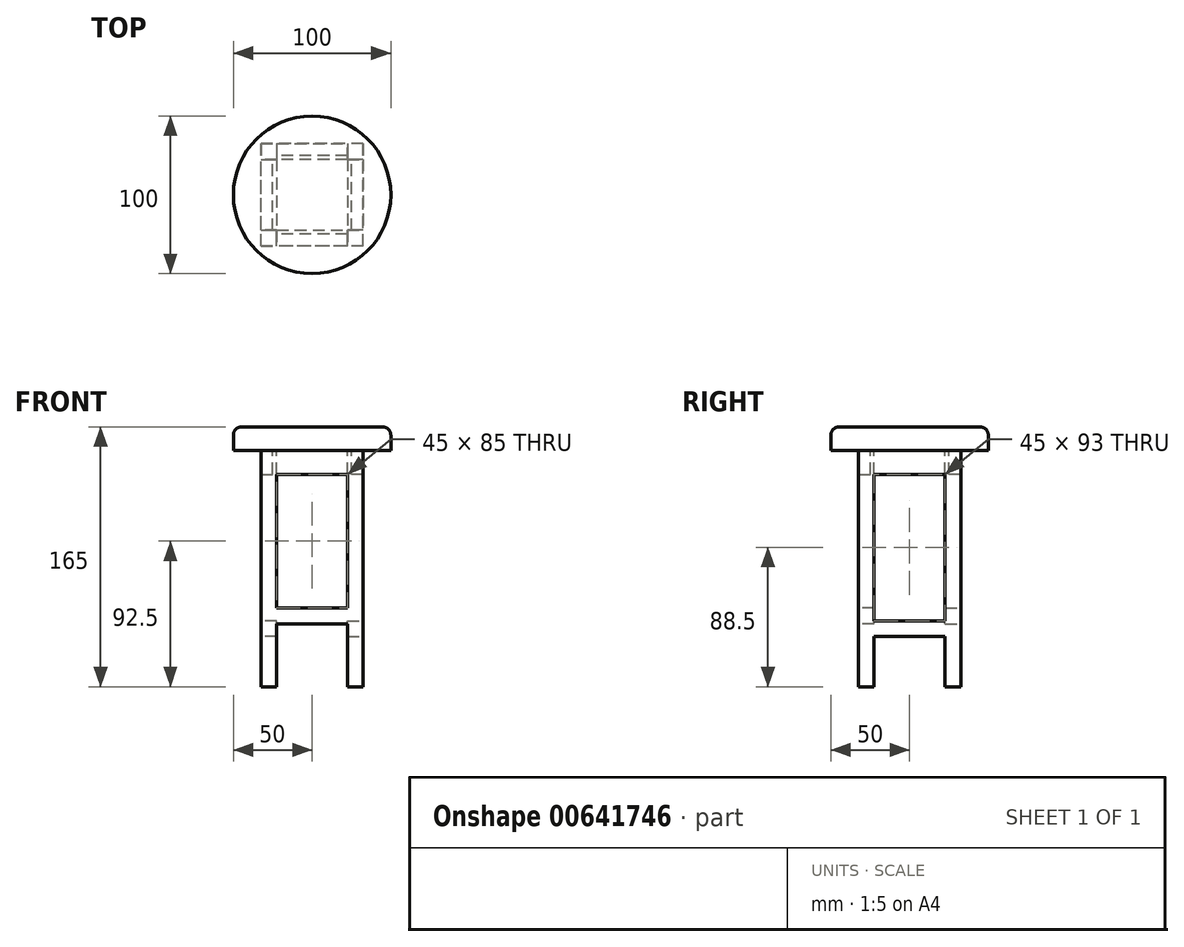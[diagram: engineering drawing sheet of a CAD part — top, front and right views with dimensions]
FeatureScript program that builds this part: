
annotation { "Feature Type Name" : "Feature", "Feature Type Description" : "" }
export const myFeature = defineFeature(function(context is Context, id is Id, definition is map)
    precondition{}
    {
        {
            var Q0;
            Q0=qCreatedBy(makeId("Top.planeOp"),FACE);
            var sketch = newSketch(context, id + "F0", { "sketchPlane" : qUnion([Q0])});
            skCircle(sketch, "E0", {"center": v(0, 0) * mm, "radius": 50 * mm});
            skSolve(sketch);
        }
        {
            var Q0;
            Q0=makeQuery(id+"F0.imprint","IMPRINT",FACE,{"disambiguationData":[TD([[makeQuery(id+"F0.imprint","IMPRINT",EDGE,{"derivedFrom":sQuery(id+"F0.wireOp",EDGE,"E0")}),1.0]])]});
            extrude(context, id + "F1", {"entities" : qUnion([Q0]), "depth" : 15 * mm, "offsetDistance" : 25 * mm});
        }
        {
            var Q0;
            Q0=makeQuery(id+"F1.opExtrude","CAP_FACE",FACE,{"disambiguationData":[OSD([sQuery(id+"F0.wireOp",EDGE,"E0")])],"isStart":true});
            var sketch = newSketch(context, id + "F2", { "sketchPlane" : qUnion([Q0])});
            skLineSegment(sketch, "E1.bottom", {"start": v(32.5, 32.5) * mm, "end": v(-32.5, 32.5) * mm});
            skLineSegment(sketch, "E1.top", {"start": v(32.5, -32.5) * mm, "end": v(-32.5, -32.5) * mm});
            skLineSegment(sketch, "E1.left", {"start": v(32.5, 32.5) * mm, "end": v(32.5, -32.5) * mm});
            skLineSegment(sketch, "E1.right", {"start": v(-32.5, 32.5) * mm, "end": v(-32.5, -32.5) * mm});
            skPoint(sketch, "E1.middle", {"position": v(0, 0) * mm});
            skLineSegment(sketch, "E2.bottom", {"start": v(-32.5, 32.5) * mm, "end": v(-22.5, 32.5) * mm});
            skLineSegment(sketch, "E2.top", {"start": v(-32.5, 22.5) * mm, "end": v(-22.5, 22.5) * mm});
            skLineSegment(sketch, "E2.left", {"start": v(-32.5, 32.5) * mm, "end": v(-32.5, 22.5) * mm});
            skLineSegment(sketch, "E2.right", {"start": v(-22.5, 32.5) * mm, "end": v(-22.5, 22.5) * mm});
            skLineSegment(sketch, "E3.bottom", {"start": v(25, 25) * mm, "end": v(-25, 25) * mm});
            skLineSegment(sketch, "E3.top", {"start": v(25, -25) * mm, "end": v(-25, -25) * mm});
            skLineSegment(sketch, "E3.left", {"start": v(25, 25) * mm, "end": v(25, -25) * mm});
            skLineSegment(sketch, "E3.right", {"start": v(-25, 25) * mm, "end": v(-25, -25) * mm});
            skLineSegment(sketch, "E4.bottom", {"start": v(32.5, 32.5) * mm, "end": v(22.5, 32.5) * mm});
            skLineSegment(sketch, "E4.top", {"start": v(32.5, 22.5) * mm, "end": v(22.5, 22.5) * mm});
            skLineSegment(sketch, "E4.left", {"start": v(32.5, 32.5) * mm, "end": v(32.5, 22.5) * mm});
            skLineSegment(sketch, "E4.right", {"start": v(22.5, 32.5) * mm, "end": v(22.5, 22.5) * mm});
            skLineSegment(sketch, "E5.bottom", {"start": v(-32.5, -32.5) * mm, "end": v(-22.5, -32.5) * mm});
            skLineSegment(sketch, "E5.top", {"start": v(-32.5, -22.5) * mm, "end": v(-22.5, -22.5) * mm});
            skLineSegment(sketch, "E5.left", {"start": v(-32.5, -32.5) * mm, "end": v(-32.5, -22.5) * mm});
            skLineSegment(sketch, "E5.right", {"start": v(-22.5, -32.5) * mm, "end": v(-22.5, -22.5) * mm});
            skLineSegment(sketch, "E6.bottom", {"start": v(32.5, -32.5) * mm, "end": v(22.5, -32.5) * mm});
            skLineSegment(sketch, "E6.top", {"start": v(32.5, -22.5) * mm, "end": v(22.5, -22.5) * mm});
            skLineSegment(sketch, "E6.left", {"start": v(32.5, -32.5) * mm, "end": v(32.5, -22.5) * mm});
            skLineSegment(sketch, "E6.right", {"start": v(22.5, -32.5) * mm, "end": v(22.5, -22.5) * mm});
            skSolve(sketch);
        }
        {
            var Q0;
            {var subQ0=sQuery(id+"F2.wireOp",EDGE,"E1.bottom");Q0=makeQuery(id+"F2.imprint","IMPRINT",FACE,{"disambiguationData":[TD([[makeQuery(id+"F2.imprint","IMPRINT",EDGE,{"derivedFrom":subQ0}),1.0]])]});}
            var Q1;
            {var subQ0=sQuery(id+"F2.wireOp",EDGE,"E1.right");Q1=makeQuery(id+"F2.imprint","IMPRINT",FACE,{"disambiguationData":[TD([[makeQuery(id+"F2.imprint","IMPRINT",EDGE,{"derivedFrom":subQ0}),1.0]])]});}
            var Q2;
            {var subQ0=sQuery(id+"F2.wireOp",EDGE,"E1.left");Q2=makeQuery(id+"F2.imprint","IMPRINT",FACE,{"disambiguationData":[TD([[makeQuery(id+"F2.imprint","IMPRINT",EDGE,{"derivedFrom":subQ0}),-1.0]])]});}
            var Q3;
            {var subQ0=sQuery(id+"F2.wireOp",EDGE,"E1.top");Q3=makeQuery(id+"F2.imprint","IMPRINT",FACE,{"disambiguationData":[TD([[makeQuery(id+"F2.imprint","IMPRINT",EDGE,{"derivedFrom":subQ0}),-1.0]])]});}
            extrude(context, id + "F3", {"entities" : qUnion([Q0, Q1, Q2, Q3]), "operationType" : NewBodyOperationType.ADD, "depth" : 15 * mm, "offsetDistance" : 25 * mm});
        }
        {
            var Q0;
            Q0=makeQuery(id+"F1.opExtrude","CAP_FACE",FACE,{"disambiguationData":[OSD([sQuery(id+"F0.wireOp",EDGE,"E0")])],"isStart":true});
            var sketch = newSketch(context, id + "F4", { "sketchPlane" : qUnion([Q0])});
            skLineSegment(sketch, "E7.bottom", {"start": v(-32.5, 32.5) * mm, "end": v(-22.5, 32.5) * mm});
            skLineSegment(sketch, "E7.top", {"start": v(-32.5, 22.5) * mm, "end": v(-22.5, 22.5) * mm});
            skLineSegment(sketch, "E7.left", {"start": v(-32.5, 32.5) * mm, "end": v(-32.5, 22.5) * mm});
            skLineSegment(sketch, "E7.right", {"start": v(-22.5, 32.5) * mm, "end": v(-22.5, 22.5) * mm});
            skLineSegment(sketch, "E8.bottom", {"start": v(32.5, 32.5) * mm, "end": v(22.5, 32.5) * mm});
            skLineSegment(sketch, "E8.top", {"start": v(32.5, 22.5) * mm, "end": v(22.5, 22.5) * mm});
            skLineSegment(sketch, "E8.left", {"start": v(32.5, 32.5) * mm, "end": v(32.5, 22.5) * mm});
            skLineSegment(sketch, "E8.right", {"start": v(22.5, 32.5) * mm, "end": v(22.5, 22.5) * mm});
            skLineSegment(sketch, "E9.bottom", {"start": v(-32.5, -32.5) * mm, "end": v(-22.5, -32.5) * mm});
            skLineSegment(sketch, "E9.top", {"start": v(-32.5, -22.5) * mm, "end": v(-22.5, -22.5) * mm});
            skLineSegment(sketch, "E9.left", {"start": v(-32.5, -32.5) * mm, "end": v(-32.5, -22.5) * mm});
            skLineSegment(sketch, "E9.right", {"start": v(-22.5, -32.5) * mm, "end": v(-22.5, -22.5) * mm});
            skLineSegment(sketch, "E10.bottom", {"start": v(32.5, -32.5) * mm, "end": v(22.5, -32.5) * mm});
            skLineSegment(sketch, "E10.top", {"start": v(32.5, -22.5) * mm, "end": v(22.5, -22.5) * mm});
            skLineSegment(sketch, "E10.left", {"start": v(32.5, -32.5) * mm, "end": v(32.5, -22.5) * mm});
            skLineSegment(sketch, "E10.right", {"start": v(22.5, -32.5) * mm, "end": v(22.5, -22.5) * mm});
            skSolve(sketch);
        }
        {
            var Q0;
            {var subQ5=sQuery(id+"F4.wireOp",EDGE,"E9.bottom");Q0=makeQuery(id+"F4.imprint","IMPRINT",FACE,{"disambiguationData":[TD([[makeQuery(id+"F4.imprint","IMPRINT",EDGE,{"derivedFrom":subQ5}),1.0]])]});}
            var Q1;
            {var subQ5=sQuery(id+"F4.wireOp",EDGE,"E7.bottom");Q1=makeQuery(id+"F4.imprint","IMPRINT",FACE,{"disambiguationData":[TD([[makeQuery(id+"F4.imprint","IMPRINT",EDGE,{"derivedFrom":subQ5}),-1.0]])]});}
            var Q2;
            {var subQ5=sQuery(id+"F4.wireOp",EDGE,"E8.bottom");Q2=makeQuery(id+"F4.imprint","IMPRINT",FACE,{"disambiguationData":[TD([[makeQuery(id+"F4.imprint","IMPRINT",EDGE,{"derivedFrom":subQ5}),1.0]])]});}
            var Q3;
            {var subQ5=sQuery(id+"F4.wireOp",EDGE,"E10.bottom");Q3=makeQuery(id+"F4.imprint","IMPRINT",FACE,{"disambiguationData":[TD([[makeQuery(id+"F4.imprint","IMPRINT",EDGE,{"derivedFrom":subQ5}),-1.0]])]});}
            extrude(context, id + "F5", {"entities" : qUnion([Q0, Q1, Q2, Q3]), "operationType" : NewBodyOperationType.ADD, "depth" : 150 * mm, "offsetDistance" : 25 * mm});
        }
        {
            var Q0;
            Q0=makeQuery(id+"F5.boolean.opBoolean","MERGE",FACE,{"derivedFrom":[makeQuery(id+"F3.opExtrude","SWEPT_FACE",FACE,{"disambiguationData":[OSD([sQuery(id+"F2.wireOp",EDGE,"E1.bottom")])]}),makeQuery(id+"F5.opExtrude","SWEPT_FACE",FACE,{"disambiguationData":[OSD([sQuery(id+"F4.wireOp",EDGE,"E7.bottom")])]}),makeQuery(id+"F5.opExtrude","SWEPT_FACE",FACE,{"disambiguationData":[OSD([sQuery(id+"F4.wireOp",EDGE,"E8.bottom")])]})]});
            var sketch = newSketch(context, id + "F6", { "sketchPlane" : qUnion([Q0])});
            skLineSegment(sketch, "E11", {"start": v(-22.5, -110) * mm, "end": v(22.5, -110) * mm});
            skLineSegment(sketch, "E12", {"start": v(22.5, -110) * mm, "end": v(22.5, -100) * mm});
            skLineSegment(sketch, "E13", {"start": v(22.5, -100) * mm, "end": v(-22.5, -100) * mm});
            skLineSegment(sketch, "E14", {"start": v(-22.5, -100) * mm, "end": v(-22.5, -110) * mm});
            skSolve(sketch);
        }
        {
            var Q0;
            Q0=makeQuery(id+"F6.imprint","IMPRINT",FACE,{"disambiguationData":[TD([[makeQuery(id+"F6.imprint","IMPRINT",EDGE,{"derivedFrom":sQuery(id+"F6.wireOp",EDGE,"E11")}),1.0]])]});
            extrude(context, id + "F7", {"entities" : qUnion([Q0]), "operationType" : NewBodyOperationType.ADD, "oppositeDirection" : true, "depth" : 10 * mm, "offsetDistance" : 25 * mm});
        }
        {
            var Q0;
            Q0=makeQuery(id+"F5.boolean.opBoolean","MERGE",FACE,{"derivedFrom":[makeQuery(id+"F3.opExtrude","SWEPT_FACE",FACE,{"disambiguationData":[OSD([sQuery(id+"F2.wireOp",EDGE,"E1.top")])]}),makeQuery(id+"F5.opExtrude","SWEPT_FACE",FACE,{"disambiguationData":[OSD([sQuery(id+"F4.wireOp",EDGE,"E9.bottom")])]}),makeQuery(id+"F5.opExtrude","SWEPT_FACE",FACE,{"disambiguationData":[OSD([sQuery(id+"F4.wireOp",EDGE,"E10.bottom")])]})]});
            var sketch = newSketch(context, id + "F8", { "sketchPlane" : qUnion([Q0])});
            skLineSegment(sketch, "E15", {"start": v(-22.5, -110) * mm, "end": v(22.5, -110) * mm});
            skLineSegment(sketch, "E16", {"start": v(22.5, -110) * mm, "end": v(22.5, -100) * mm});
            skLineSegment(sketch, "E17", {"start": v(22.5, -100) * mm, "end": v(-22.5, -100) * mm});
            skLineSegment(sketch, "E18", {"start": v(-22.5, -100) * mm, "end": v(-22.5, -110) * mm});
            skSolve(sketch);
        }
        {
            var Q0;
            Q0=makeQuery(id+"F8.imprint","IMPRINT",FACE,{"disambiguationData":[TD([[makeQuery(id+"F8.imprint","IMPRINT",EDGE,{"derivedFrom":sQuery(id+"F8.wireOp",EDGE,"E15")}),1.0]])]});
            extrude(context, id + "F9", {"entities" : qUnion([Q0]), "operationType" : NewBodyOperationType.ADD, "oppositeDirection" : true, "depth" : 10 * mm, "offsetDistance" : 25 * mm});
        }
        {
            var Q0;
            Q0=makeQuery(id+"F5.boolean.opBoolean","MERGE",FACE,{"derivedFrom":[makeQuery(id+"F3.opExtrude","SWEPT_FACE",FACE,{"disambiguationData":[OSD([sQuery(id+"F2.wireOp",EDGE,"E1.right")])]}),makeQuery(id+"F5.opExtrude","SWEPT_FACE",FACE,{"disambiguationData":[OSD([sQuery(id+"F4.wireOp",EDGE,"E7.left")])]}),makeQuery(id+"F5.opExtrude","SWEPT_FACE",FACE,{"disambiguationData":[OSD([sQuery(id+"F4.wireOp",EDGE,"E9.left")])]})]});
            var sketch = newSketch(context, id + "F10", { "sketchPlane" : qUnion([Q0])});
            skLineSegment(sketch, "E19", {"start": v(-22.5, -118) * mm, "end": v(22.5, -118) * mm});
            skLineSegment(sketch, "E20", {"start": v(22.5, -118) * mm, "end": v(22.5, -108) * mm});
            skLineSegment(sketch, "E21", {"start": v(22.5, -108) * mm, "end": v(-22.5, -108) * mm});
            skLineSegment(sketch, "E22", {"start": v(-22.5, -108) * mm, "end": v(-22.5, -118) * mm});
            skSolve(sketch);
        }
        {
            var Q0;
            Q0=makeQuery(id+"F10.imprint","IMPRINT",FACE,{"disambiguationData":[TD([[makeQuery(id+"F10.imprint","IMPRINT",EDGE,{"derivedFrom":sQuery(id+"F10.wireOp",EDGE,"E19")}),1.0]])]});
            extrude(context, id + "F11", {"entities" : qUnion([Q0]), "operationType" : NewBodyOperationType.ADD, "oppositeDirection" : true, "depth" : 10 * mm, "offsetDistance" : 25 * mm});
        }
        {
            var Q0;
            Q0=makeQuery(id+"F5.boolean.opBoolean","MERGE",FACE,{"derivedFrom":[makeQuery(id+"F3.opExtrude","SWEPT_FACE",FACE,{"disambiguationData":[OSD([sQuery(id+"F2.wireOp",EDGE,"E1.left")])]}),makeQuery(id+"F5.opExtrude","SWEPT_FACE",FACE,{"disambiguationData":[OSD([sQuery(id+"F4.wireOp",EDGE,"E8.left")])]}),makeQuery(id+"F5.opExtrude","SWEPT_FACE",FACE,{"disambiguationData":[OSD([sQuery(id+"F4.wireOp",EDGE,"E10.left")])]})]});
            var sketch = newSketch(context, id + "F12", { "sketchPlane" : qUnion([Q0])});
            skLineSegment(sketch, "E23", {"start": v(-22.5, -118) * mm, "end": v(22.5, -118) * mm});
            skLineSegment(sketch, "E24", {"start": v(22.5, -118) * mm, "end": v(22.5, -108) * mm});
            skLineSegment(sketch, "E25", {"start": v(22.5, -108) * mm, "end": v(-22.5, -108) * mm});
            skLineSegment(sketch, "E26", {"start": v(-22.5, -108) * mm, "end": v(-22.5, -118) * mm});
            skSolve(sketch);
        }
        {
            var Q0;
            Q0=makeQuery(id+"F12.imprint","IMPRINT",FACE,{"disambiguationData":[TD([[makeQuery(id+"F12.imprint","IMPRINT",EDGE,{"derivedFrom":sQuery(id+"F12.wireOp",EDGE,"E23")}),1.0]])]});
            extrude(context, id + "F13", {"entities" : qUnion([Q0]), "operationType" : NewBodyOperationType.ADD, "oppositeDirection" : true, "depth" : 10 * mm, "offsetDistance" : 25 * mm});
        }
        {
            var Q0;
            Q0=makeQuery(id+"F1.opExtrude","CAP_EDGE",EDGE,{"disambiguationData":[OSD([sQuery(id+"F0.wireOp",EDGE,"E0")])],"isStart":false});
            fillet(context, id + "F14", {"entities" : qUnion([Q0]), "radius" : 5 * mm, "tangentPropagation" : true, "allowEdgeOverflow" : false});
        }
    });
